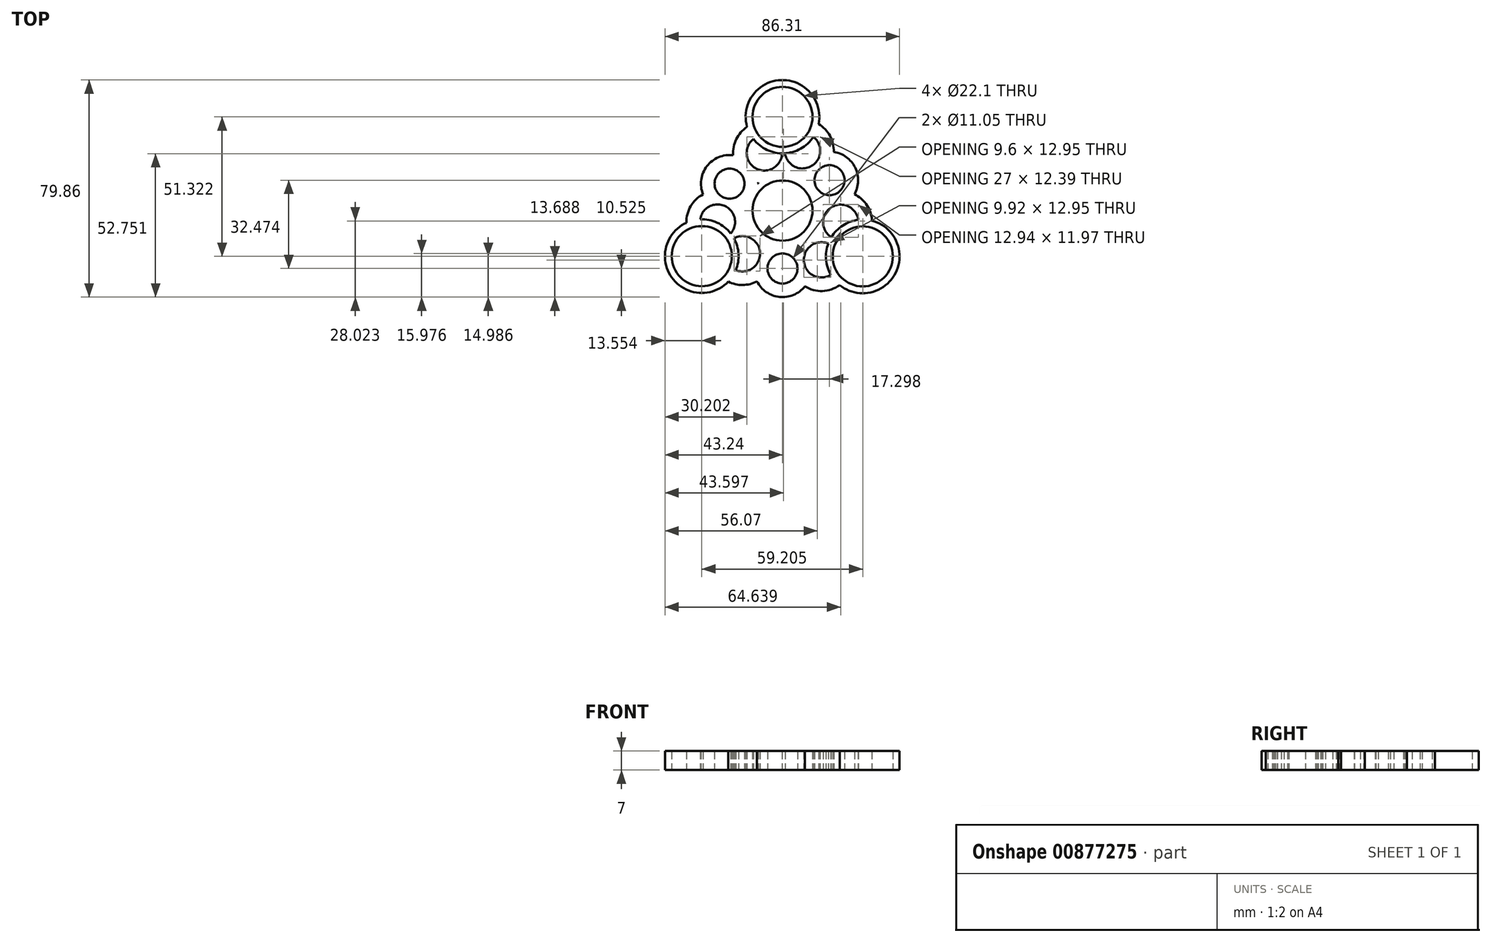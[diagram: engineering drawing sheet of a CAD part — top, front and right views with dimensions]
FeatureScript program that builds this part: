
annotation { "Feature Type Name" : "Feature", "Feature Type Description" : "" }
export const myFeature = defineFeature(function(context is Context, id is Id, definition is map)
    precondition{}
    {
        {
            var Q0;
            Q0=qCreatedBy(makeId("Top.planeOp"),FACE);
            var sketch = newSketch(context, id + "F0", { "sketchPlane" : qUnion([Q0])});
            skCircle(sketch, "E0", {"center": v(0, 0) * mm, "radius": 11.05 * mm});
            skCircle(sketch, "E1", {"center": v(0, 34.47) * mm, "radius": 11.05 * mm});
            skArc(sketch, "E2", {"start": v(-0.18, 20.92) * mm, "mid": v(0.39, 20.92) * mm, "end": v(0.95, 20.95) * mm});
            skCircle(sketch, "E3.1.0", {"center": v(-29.69, -16.76) * mm, "radius": 13.55 * mm});
            skCircle(sketch, "E3.1.1", {"center": v(-29.69, -16.76) * mm, "radius": 11.05 * mm});
            skCircle(sketch, "E3.2.0", {"center": v(29.52, -16.85) * mm, "radius": 13.55 * mm});
            skCircle(sketch, "E3.2.1", {"center": v(29.52, -16.85) * mm, "radius": 11.05 * mm});
            skPoint(sketch, "E3.center", {"position": v(-0.06, 0.29) * mm});
            skCircle(sketch, "E4", {"center": v(0, -21.31) * mm, "radius": 5.52 * mm});
            skArc(sketch, "E5", {"start": v(16.82, -12.12) * mm, "mid": v(7.87, -18.68) * mm, "end": v(17.8, -23.64) * mm});
            skArc(sketch, "E6", {"start": v(-17.16, -21.92) * mm, "mid": v(-8.24, -15.5) * mm, "end": v(-17.84, -10.18) * mm});
            skArc(sketch, "E7.1.0", {"start": v(27.87, -3.4) * mm, "mid": v(17.86, 1.12) * mm, "end": v(18.05, -9.86) * mm});
            skArc(sketch, "E7.2.0", {"start": v(-10.68, 26.33) * mm, "mid": v(-9.59, 15.4) * mm, "end": v(-0.17, 21.06) * mm});
            skPoint(sketch, "E7.center", {"position": v(0.01, 0.34) * mm});
            skCircle(sketch, "E8.1.0", {"center": v(17.3, 11.16) * mm, "radius": 5.52 * mm});
            skArc(sketch, "E8.1.1", {"start": v(0.9, 21.41) * mm, "mid": v(10.81, 16.48) * mm, "end": v(10.73, 27.55) * mm});
            skCircle(sketch, "E8.2.0", {"center": v(-19.47, 9.9) * mm, "radius": 5.52 * mm});
            skArc(sketch, "E8.2.1", {"start": v(-19.02, -8.4) * mm, "mid": v(-21.2, 1.68) * mm, "end": v(-30.27, -3.22) * mm});
            skPoint(sketch, "E8.center", {"position": v(-0.73, -0.08) * mm});
            skArc(sketch, "E9.0", {"start": v(-13.04, 30.79) * mm, "mid": v(-17, 26.26) * mm, "end": v(-18.14, 20.34) * mm});
            skArc(sketch, "E10.0", {"start": v(-13.72, 1.09) * mm, "mid": v(-13.6, 1.17) * mm, "end": v(-13.5, 1.24) * mm});
            skArc(sketch, "E11.0", {"start": v(-17.27, -13.52) * mm, "mid": v(-16.96, -13.29) * mm, "end": v(-16.65, -13.05) * mm});
            skArc(sketch, "E12.trimOffspring", {"start": v(-29.22, 5.96) * mm, "mid": v(-33.76, 1.63) * mm, "end": v(-35.34, -4.44) * mm});
            skArc(sketch, "E13.trimOffspring", {"start": v(-8.95, 10.17) * mm, "mid": v(-9.05, 10.08) * mm, "end": v(-9.16, 9.98) * mm});
            skArc(sketch, "E14.trimOffspring", {"start": v(-9.16, 9.98) * mm, "mid": v(-9.05, 9.96) * mm, "end": v(-8.95, 9.94) * mm});
            skArc(sketch, "E15.trimOffspring", {"start": v(-8.95, 9.94) * mm, "mid": v(-8.95, 10.06) * mm, "end": v(-8.95, 10.17) * mm});
            skArc(sketch, "E16.trimOffspring", {"start": v(-18.14, 20.34) * mm, "mid": v(-27.8, 16.33) * mm, "end": v(-29.22, 5.96) * mm});
            skArc(sketch, "E17.trimOffspring", {"start": v(-13.53, 0.7) * mm, "mid": v(-13.63, 0.9) * mm, "end": v(-13.72, 1.09) * mm});
            skArc(sketch, "E18.0", {"start": v(-19.92, -26.15) * mm, "mid": v(-14.64, -27.39) * mm, "end": v(-9.39, -26.07) * mm});
            skArc(sketch, "E19.0", {"start": v(-9.39, -26.07) * mm, "mid": v(-1.07, -31.78) * mm, "end": v(8.23, -27.87) * mm});
            skArc(sketch, "E20.trimOffspring", {"start": v(8.23, -27.87) * mm, "mid": v(14.7, -29.6) * mm, "end": v(21.04, -27.42) * mm});
            skArc(sketch, "E21.0", {"start": v(32.82, -2.75) * mm, "mid": v(30.75, 2.43) * mm, "end": v(26.48, 6.02) * mm});
            skArc(sketch, "E22.trimOffspring", {"start": v(18.86, 21.57) * mm, "mid": v(17.47, 27.45) * mm, "end": v(13.29, 31.82) * mm});
            skArc(sketch, "E23.trimOffspring", {"start": v(26.48, 6.02) * mm, "mid": v(26.75, 15.8) * mm, "end": v(18.86, 21.57) * mm});
            skArc(sketch, "E24", {"start": v(32.82, -3.71) * mm, "mid": v(32.83, -3.23) * mm, "end": v(32.82, -2.75) * mm});
            skArc(sketch, "E25.trimOffspring", {"start": v(11.38, 27.1) * mm, "mid": v(2.02, 47.87) * mm, "end": v(-13.04, 30.79) * mm});
            skArc(sketch, "E26", {"start": v(-13.04, 30.79) * mm, "mid": v(-12.07, 28.45) * mm, "end": v(-10.68, 26.33) * mm});
            skArc(sketch, "E27", {"start": v(-10.68, 26.33) * mm, "mid": v(0.55, 21.04) * mm, "end": v(11.38, 27.1) * mm});
            skSolve(sketch);
        }
        {
            var Q0;
            Q0=makeQuery(id+"F0.imprint","IMPRINT",FACE,{"disambiguationData":[TD([[makeQuery(id+"F0.imprint","IMPRINT",EDGE,{"derivedFrom":sQuery(id+"F0.wireOp",EDGE,"E3.1.1")}),-1.0]])]});
            var Q1;
            Q1=makeQuery(id+"F0.imprint","IMPRINT",FACE,{"disambiguationData":[TD([[makeQuery(id+"F0.imprint","IMPRINT",EDGE,{"derivedFrom":sQuery(id+"F0.wireOp",EDGE,"E1")}),-1.0]])]});
            var Q2;
            Q2=makeQuery(id+"F0.imprint","IMPRINT",FACE,{"disambiguationData":[TD([[makeQuery(id+"F0.imprint","IMPRINT",EDGE,{"derivedFrom":sQuery(id+"F0.wireOp",EDGE,"E0")}),-1.0]])]});
            var Q3;
            Q3=makeQuery(id+"F0.imprint","IMPRINT",FACE,{"disambiguationData":[TD([[makeQuery(id+"F0.imprint","IMPRINT",EDGE,{"derivedFrom":sQuery(id+"F0.wireOp",EDGE,"E3.2.1")}),-1.0]])]});
            extrude(context, id + "F1", {"entities" : qUnion([Q0, Q1, Q2, Q3]), "depth" : 7 * mm, "offsetDistance" : 25 * mm});
        }
    });
